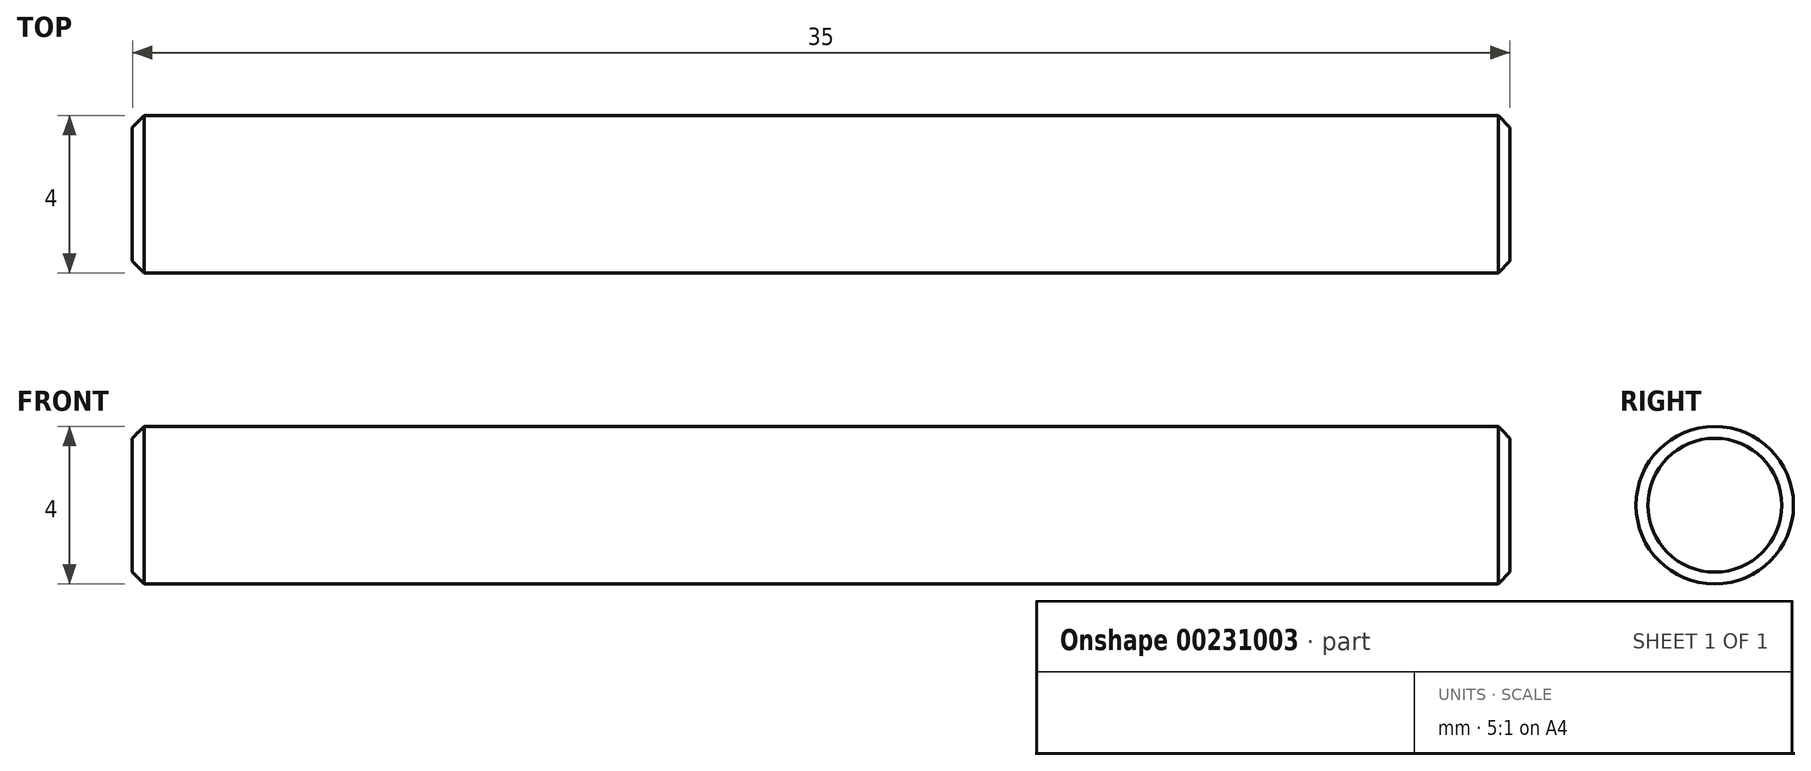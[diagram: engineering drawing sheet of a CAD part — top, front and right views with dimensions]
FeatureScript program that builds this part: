
annotation { "Feature Type Name" : "Feature", "Feature Type Description" : "" }
export const myFeature = defineFeature(function(context is Context, id is Id, definition is map)
    precondition{}
    {
        {
            var Q0;
            Q0=qCreatedBy(makeId("Top.planeOp"),FACE);
            var sketch = newSketch(context, id + "F0", { "sketchPlane" : qUnion([Q0])});
            skLineSegment(sketch, "E0", {"start": v(0, 0) * mm, "end": v(45, 0) * mm, "construction": true});
            skLineSegment(sketch, "E1", {"start": v(3.8, 0) * mm, "end": v(38.8, 0) * mm, "construction": true});
            skLineSegment(sketch, "E2.bottom", {"start": v(3.8, 0) * mm, "end": v(38.8, 0) * mm});
            skLineSegment(sketch, "E2.top", {"start": v(3.8, 2) * mm, "end": v(38.8, 2) * mm});
            skLineSegment(sketch, "E2.left", {"start": v(3.8, 0) * mm, "end": v(3.8, 2) * mm});
            skLineSegment(sketch, "E2.right", {"start": v(38.8, 0) * mm, "end": v(38.8, 2) * mm});
            skSolve(sketch);
        }
        {
            var Q0;
            Q0=makeQuery(id+"F0.imprint","IMPRINT",FACE,{"disambiguationData":[TD([[makeQuery(id+"F0.imprint","IMPRINT",EDGE,{"derivedFrom":sQuery(id+"F0.wireOp",EDGE,"E2.bottom")}),1.0]])]});
            var Q1;
            Q1=sQuery(id+"F0.wireOp",EDGE,"E0");
            revolve(context, id + "F1", {"entities" : qUnion([Q0]), "axis" : qUnion([Q1]), "revolveType" : RevolveType.FULL});
        }
        {
            var Q0;
            Q0=makeQuery(id+"F1.opRevolve","SWEPT_EDGE",EDGE,{"disambiguationData":[OSD([sQuery(id+"F0.wireOp",EDGE,"E2.top"),sQuery(id+"F0.wireOp",EDGE,"E2.right")])]});
            var Q1;
            Q1=makeQuery(id+"F1.opRevolve","SWEPT_EDGE",EDGE,{"disambiguationData":[OSD([sQuery(id+"F0.wireOp",EDGE,"E2.top"),sQuery(id+"F0.wireOp",EDGE,"E2.left")])]});
            chamfer(context, id + "F2", {"entities" : qUnion([Q0, Q1]), "width" : 0.3 * mm, "tangentPropagation" : true});
        }
    });
